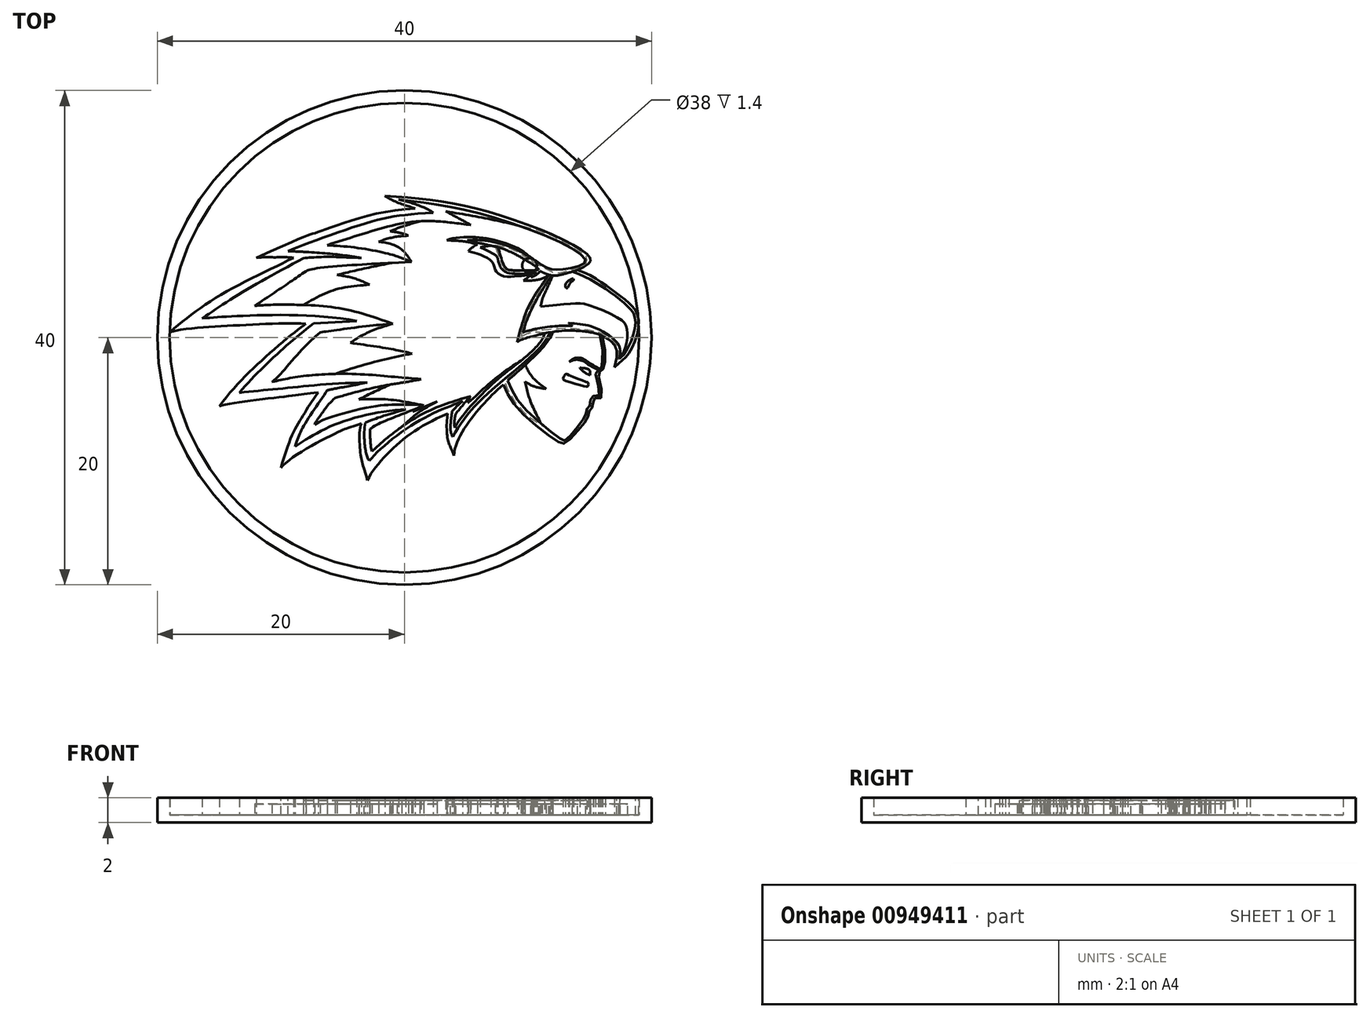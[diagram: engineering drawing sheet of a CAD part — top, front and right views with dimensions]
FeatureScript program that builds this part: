
annotation { "Feature Type Name" : "Feature", "Feature Type Description" : "" }
export const myFeature = defineFeature(function(context is Context, id is Id, definition is map)
    precondition{}
    {
        {
            var Q0;
            Q0=qCreatedBy(makeId("Top.planeOp"),FACE);
            var sketch = newSketch(context, id + "F0", { "sketchPlane" : qUnion([Q0])});
            skCircle(sketch, "E0", {"center": v(0, 0) * mm, "radius": 20 * mm});
            skSolve(sketch);
        }
        {
            var Q0;
            Q0=makeQuery(id+"F0.imprint","IMPRINT",FACE,{"disambiguationData":[TD([[makeQuery(id+"F0.imprint","IMPRINT",EDGE,{"derivedFrom":sQuery(id+"F0.wireOp",EDGE,"E0")}),1.0]])]});
            extrude(context, id + "F1", {"entities" : qUnion([Q0]), "oppositeDirection" : true, "depth" : 0.6 * mm, "offsetDistance" : 25 * mm});
        }
        {
            var Q0;
            Q0=qCreatedBy(makeId("Top.planeOp"),FACE);
            var sketch = newSketch(context, id + "F2", { "sketchPlane" : qUnion([Q0])});
            skCircle(sketch, "E1", {"center": v(0, 0) * mm, "radius": 20 * mm});
            skCircle(sketch, "E2", {"center": v(0, 0) * mm, "radius": 19 * mm});
            skSolve(sketch);
        }
        {
            var Q0;
            Q0=makeQuery(id+"F2.imprint","IMPRINT",FACE,{"disambiguationData":[TD([[makeQuery(id+"F2.imprint","IMPRINT",EDGE,{"derivedFrom":sQuery(id+"F2.wireOp",EDGE,"E1")}),1.0]])]});
            extrude(context, id + "F3", {"entities" : qUnion([Q0]), "operationType" : NewBodyOperationType.ADD, "depth" : 1.4 * mm, "offsetDistance" : 25 * mm});
        }
        {
            var Q0;
            Q0=qCreatedBy(makeId("Top.planeOp"),FACE);
            var sketch = newSketch(context, id + "F4", { "sketchPlane" : qUnion([Q0])});
            skFitSpline(sketch, "E3", {"points": [v(-1.58, 11.46) * mm, v(7.72, 9.91) * mm, v(15.05, 6.42) * mm, v(14, 5.46) * mm], "startDerivative": vector(21.52, -1.26) * mm, "endDerivative": vector(-13.3, -6.93) * mm});
            skFitSpline(sketch, "E4", {"points": [v(3.5, -6.16) * mm, v(-0.78, -8.83) * mm, v(-3, -11.54) * mm], "startDerivative": vector(-10.76, -4.46) * mm, "endDerivative": vector(-2.73, -5.76) * mm});
            skFitSpline(sketch, "E5", {"points": [v(-3, -11.54) * mm, v(-3.55, -9.5) * mm, v(-3.5, -6.96) * mm], "startDerivative": vector(-2.35, 7.78) * mm, "endDerivative": vector(1.35, 3.27) * mm});
            skFitSpline(sketch, "E6", {"points": [v(-3.5, -6.96) * mm, v(-5.27, -7.6) * mm, v(-10, -10.54) * mm], "startDerivative": vector(-9.15, -3.1) * mm, "endDerivative": vector(-2.97, -4.21) * mm});
            skFitSpline(sketch, "E7", {"points": [v(-10, -10.54) * mm, v(-8.32, -6.48) * mm, v(-7, -4.44) * mm], "startDerivative": vector(3.25, 11.93) * mm, "endDerivative": vector(2.66, 3.7) * mm});
            skFitSpline(sketch, "E8", {"points": [v(-7, -4.44) * mm, v(-9.47, -4.75) * mm, v(-15, -5.54) * mm], "startDerivative": vector(-8.24, -0.84) * mm, "endDerivative": vector(-4.12, -1.43) * mm});
            skFitSpline(sketch, "E9", {"points": [v(-15, -5.54) * mm, v(-11, -1.34) * mm, v(-8, 1.1) * mm], "startDerivative": vector(6.54, 8.64) * mm, "endDerivative": vector(3.53, 2.33) * mm});
            skFitSpline(sketch, "E10", {"points": [v(-8, 1.1) * mm, v(-13.7, 0.98) * mm, v(-19, 0.46) * mm], "startDerivative": vector(-8.4, 0.77) * mm, "endDerivative": vector(-10.04, -2.22) * mm});
            skFitSpline(sketch, "E11", {"points": [v(-19, 0.46) * mm, v(-14.13, 3.88) * mm, v(-8, 7.06) * mm], "startDerivative": vector(8.8, 7.31) * mm, "endDerivative": vector(6.6, 4.65) * mm});
            skFitSpline(sketch, "E12", {"points": [v(-12, 6.46) * mm, v(-6.88, 8.58) * mm, v(0.86, 10.46) * mm], "startDerivative": vector(30.08, 13.67) * mm, "endDerivative": vector(18.85, 0.85) * mm});
            skFitSpline(sketch, "E13", {"points": [v(0.86, 10.46) * mm, v(-0.78, 11.03) * mm, v(-1.58, 11.46) * mm], "startDerivative": vector(-2.07, 0.66) * mm, "endDerivative": vector(-0.97, 0.57) * mm});
            skFitSpline(sketch, "E14", {"points": [v(3.5, -6.16) * mm, v(3.53, -8.34) * mm, v(4, -9.54) * mm], "startDerivative": vector(-0.77, -3.97) * mm, "endDerivative": vector(1.6, -4.4) * mm});
            skFitSpline(sketch, "E15", {"points": [v(4, -9.54) * mm, v(5.91, -5.93) * mm, v(9.09, -2.82) * mm, v(12, 0.46) * mm], "startDerivative": vector(0.54, 10.48) * mm, "endDerivative": vector(2.95, 8.84) * mm});
            skFitSpline(sketch, "E16", {"points": [v(-9, 6.46) * mm, v(-10.52, 6.5) * mm, v(-12, 6.46) * mm], "startDerivative": vector(-3.14, 0.42) * mm, "endDerivative": vector(-2.86, -0.43) * mm});
            skFitSpline(sketch, "E17", {"points": [v(14, 5.46) * mm, v(16.43, 4.12) * mm, v(18.07, 2.88) * mm, v(18.94, 1.52) * mm, v(18.18, -1.26) * mm, v(17, -2.4) * mm], "startDerivative": vector(12.4, -3.48) * mm, "endDerivative": vector(-8.18, -8.07) * mm});
            skFitSpline(sketch, "E18", {"points": [v(17, -2.4) * mm, v(17.07, -0.75) * mm, v(15.73, 0.25) * mm, v(14.63, 0.5) * mm, v(12, 0.46) * mm], "startDerivative": vector(1.76, 6.26) * mm, "endDerivative": vector(-11.27, -1.86) * mm});
            skFitSpline(sketch, "E19", {"points": [v(11, 5.38) * mm, v(9.78, 6.3) * mm, v(7, 7.43) * mm], "startDerivative": vector(-2.8, 3.17) * mm, "endDerivative": vector(-5.7, 0.83) * mm});
            skFitSpline(sketch, "E20", {"points": [v(7, 7.43) * mm, v(7.74, 5.78) * mm, v(8, 5.43) * mm, v(8.44, 5.22) * mm, v(10.45, 5.2) * mm, v(10.9, 5.29) * mm, v(11, 5.38) * mm], "startDerivative": vector(6.03, -7.57) * mm, "endDerivative": vector(2.14, 2.82) * mm});
            skCircle(sketch, "E21", {"center": v(10.12, 5.84) * mm, "radius": 0.6 * mm});
            skFitSpline(sketch, "E22", {"points": [v(8, -3.8) * mm, v(9.3, -5.87) * mm, v(12.45, -8.44) * mm, v(13, -8.54) * mm, v(14.39, -7.12) * mm, v(14.92, -6.25) * mm, v(15.02, -5.8) * mm, v(15.28, -5.52) * mm, v(15.34, -4.9) * mm, v(15.93, -4.86) * mm, v(15.7, -2.86) * mm, v(15.92, -2.64) * mm, v(16.14, -2.4) * mm, v(16, 0.14) * mm], "startDerivative": vector(7.5, -17.46) * mm, "endDerivative": vector(-8.07, 26.27) * mm});
            skFitSpline(sketch, "E23", {"points": [v(15.02, -3.03) * mm, v(14.56, -2.8) * mm, v(14.2, -2.44) * mm], "startDerivative": vector(-1.12, 0.33) * mm, "endDerivative": vector(-0.33, 0.79) * mm});
            skFitSpline(sketch, "E24", {"points": [v(14.2, -2.44) * mm, v(14.57, -2.47) * mm, v(14.94, -2.61) * mm, v(15.04, -2.8) * mm, v(15.02, -3.03) * mm], "startDerivative": vector(1.37, -0.38) * mm, "endDerivative": vector(-0.15, -0.97) * mm});
            skFitSpline(sketch, "E25", {"points": [v(15.68, -2.55) * mm, v(15.48, -2.5) * mm, v(14.93, -2.22) * mm, v(14.67, -2.02) * mm, v(14.03, -1.79) * mm, v(13.34, -1.95) * mm], "startDerivative": vector(-2.24, 0.34) * mm, "endDerivative": vector(-2.61, -1.2) * mm});
            skFitSpline(sketch, "E26", {"points": [v(13.34, -1.95) * mm, v(13.86, -1.65) * mm, v(14.3, -1.65) * mm, v(14.57, -1.77) * mm, v(15.1, -2.13) * mm, v(15.55, -2.4) * mm, v(15.89, -2.49) * mm], "startDerivative": vector(2.26, 2.4) * mm, "endDerivative": vector(2.1, 0.6) * mm});
            skFitSpline(sketch, "E27", {"points": [v(15.68, -2.55) * mm, v(15.8, -2.54) * mm, v(15.89, -2.49) * mm], "startDerivative": vector(0.25, -0.06) * mm, "endDerivative": vector(0.25, 0.3) * mm});
            skFitSpline(sketch, "E28", {"points": [v(14.52, -3.93) * mm, v(12.97, -3.46) * mm, v(12.85, -3.33) * mm, v(12.9, -3.2) * mm, v(12.98, -3) * mm, v(13.07, -2.94) * mm, v(13.22, -3) * mm, v(14.68, -3.57) * mm, v(14.86, -3.66) * mm, v(14.9, -3.76) * mm, v(14.84, -3.93) * mm, v(14.78, -3.97) * mm, v(14.52, -3.93) * mm]});
            skFitSpline(sketch, "E29", {"points": [v(12, 0.46) * mm, v(10.73, 0.2) * mm, v(9.12, -0.4) * mm], "startDerivative": vector(-4.79, -0.65) * mm, "endDerivative": vector(-1.75, -1.76) * mm});
            skFitSpline(sketch, "E30", {"points": [v(9.12, -0.4) * mm, v(10.04, 2.5) * mm, v(11.7, 5.07) * mm], "startDerivative": vector(1.47, 5.98) * mm, "endDerivative": vector(3.7, 4.95) * mm});
            skFitSpline(sketch, "E31", {"points": [v(14, 5.46) * mm, v(12.41, 5.04) * mm, v(11.7, 5.07) * mm, v(11, 5.38) * mm], "startDerivative": vector(-4.1, -1.19) * mm, "endDerivative": vector(-2.43, 1.23) * mm});
            skFitSpline(sketch, "E32", {"points": [v(7, 7.43) * mm, v(5.97, 7.67) * mm, v(5.07, 7.87) * mm], "startDerivative": vector(-2.03, 0.53) * mm, "endDerivative": vector(-1.84, 0.4) * mm});
            skFitSpline(sketch, "E33", {"points": [v(5.07, 7.87) * mm, v(6.4, 7.87) * mm, v(9.35, 7) * mm, v(11.6, 5.62) * mm, v(12.86, 5.54) * mm, v(14.66, 6.18) * mm, v(7.76, 9.56) * mm, v(-0.49, 11.17) * mm], "startDerivative": vector(13.05, 0.9) * mm, "endDerivative": vector(-32.62, 3.92) * mm});
            skFitSpline(sketch, "E34", {"points": [v(-0.49, 11.17) * mm, v(0.93, 10.77) * mm, v(2.33, 10.11) * mm], "startDerivative": vector(2.94, -0.6) * mm, "endDerivative": vector(1.78, -1.4) * mm});
            skFitSpline(sketch, "E35", {"points": [v(2.33, 10.11) * mm, v(-3.07, 9.27) * mm, v(-9.44, 7) * mm], "startDerivative": vector(-15.85, -1) * mm, "endDerivative": vector(-7.4, -3.02) * mm});
            skFitSpline(sketch, "E36", {"points": [v(-9.44, 7) * mm, v(-6.18, 6.8) * mm, v(-3.48, 6.46) * mm], "startDerivative": vector(6.38, -0.27) * mm, "endDerivative": vector(5.53, -0.87) * mm});
            skFitSpline(sketch, "E37", {"points": [v(-3.48, 6.46) * mm, v(-6.21, 6.54) * mm, v(-8.18, 6.43) * mm], "startDerivative": vector(-6.33, 0.08) * mm, "endDerivative": vector(-3.05, -0.33) * mm});
            skFitSpline(sketch, "E38", {"points": [v(-8.18, 6.43) * mm, v(-13.5, 3.44) * mm, v(-16.37, 1.55) * mm], "startDerivative": vector(-9.86, -5.27) * mm, "endDerivative": vector(-6.1, -4.23) * mm});
            skFitSpline(sketch, "E39", {"points": [v(-16.37, 1.55) * mm, v(-13.5, 1.75) * mm, v(-3.85, 1.35) * mm], "startDerivative": vector(6.8, 0.6) * mm, "endDerivative": vector(14.41, -2.83) * mm});
            skFitSpline(sketch, "E40", {"points": [v(-3.85, 1.35) * mm, v(-7.35, 1.14) * mm], "startDerivative": vector(-3.5, -0.2) * mm, "endDerivative": vector(-3.5, -0.2) * mm});
            skFitSpline(sketch, "E41", {"points": [v(-7.35, 1.14) * mm, v(-10.41, -1.43) * mm, v(-13.36, -4.46) * mm], "startDerivative": vector(-6.68, -4.88) * mm, "endDerivative": vector(-5.36, -6.32) * mm});
            skFitSpline(sketch, "E42", {"points": [v(-13.36, -4.46) * mm, v(-9.36, -4.06) * mm, v(-3.02, -3.64) * mm], "startDerivative": vector(8.78, 0.94) * mm, "endDerivative": vector(14.42, 0.16) * mm});
            skFitSpline(sketch, "E43", {"points": [v(-3.02, -3.64) * mm, v(-5.54, -4.12) * mm, v(-6.24, -4.25) * mm], "startDerivative": vector(-4.48, -0.91) * mm, "endDerivative": vector(-1.64, -0.24) * mm});
            skFitSpline(sketch, "E44", {"points": [v(-6.24, -4.25) * mm, v(-8.21, -7.25) * mm, v(-8.87, -8.8) * mm], "startDerivative": vector(-3.02, -4.33) * mm, "endDerivative": vector(-1.83, -4.96) * mm});
            skFitSpline(sketch, "E45", {"points": [v(-8.87, -8.8) * mm, v(-5.6, -7.02) * mm, v(0.1, -5.81) * mm], "startDerivative": vector(6.74, 4.12) * mm, "endDerivative": vector(9.55, 0.33) * mm});
            skFitSpline(sketch, "E46", {"points": [v(0.1, -5.81) * mm, v(-1.02, -6.13) * mm, v(-3.18, -6.9) * mm], "startDerivative": vector(-4.07, -1.11) * mm, "endDerivative": vector(-5.58, -2.4) * mm});
            skFitSpline(sketch, "E47", {"points": [v(-3.18, -6.9) * mm, v(-3.14, -9.14) * mm, v(-2.84, -9.97) * mm], "startDerivative": vector(-0.7, -4.41) * mm, "endDerivative": vector(1.32, -1.52) * mm});
            skFitSpline(sketch, "E48", {"points": [v(-2.84, -9.97) * mm, v(0.78, -6.97) * mm, v(4.7, -5.14) * mm], "startDerivative": vector(3.54, 4.6) * mm, "endDerivative": vector(7.5, 2.99) * mm});
            skFitSpline(sketch, "E49", {"points": [v(4.7, -5.14) * mm, v(3.85, -5.96) * mm], "startDerivative": vector(-1.54, -1.24) * mm, "endDerivative": vector(-0.85, -0.81) * mm});
            skFitSpline(sketch, "E50", {"points": [v(3.85, -5.96) * mm, v(3.74, -7.58) * mm, v(3.91, -8.04) * mm], "startDerivative": vector(-0.38, -2.91) * mm, "endDerivative": vector(0.59, -1.08) * mm});
            skFitSpline(sketch, "E51", {"points": [v(3.91, -8.04) * mm, v(5.56, -5.69) * mm, v(8.66, -2.88) * mm, v(11.8, 0.43) * mm], "startDerivative": vector(4.66, 8.5) * mm, "endDerivative": vector(3.92, 9.27) * mm});
            skFitSpline(sketch, "E52", {"points": [v(11.8, 0.43) * mm, v(12, 0.46) * mm], "startDerivative": vector(0.2, 0.03) * mm, "endDerivative": vector(0.2, 0.03) * mm});
            skFitSpline(sketch, "E53", {"points": [v(11.92, 5.03) * mm, v(10.4, 2.5) * mm, v(9.6, 0.43) * mm], "startDerivative": vector(-3.21, -4.76) * mm, "endDerivative": vector(-1.06, -4.44) * mm});
            skFitSpline(sketch, "E54", {"points": [v(9.6, 0.43) * mm, v(10.45, 0.67) * mm, v(12.21, 0.92) * mm, v(13.6, 0.96) * mm], "startDerivative": vector(2.74, 0.91) * mm, "endDerivative": vector(3.8, 0) * mm});
            skFitSpline(sketch, "E55", {"points": [v(13.6, 0.96) * mm, v(13.29, 1.17) * mm], "startDerivative": vector(-0.45, 0.21) * mm, "endDerivative": vector(-0.45, 0.21) * mm});
            skFitSpline(sketch, "E56", {"points": [v(13.29, 1.17) * mm, v(14.52, 1.05) * mm, v(15.83, 0.62) * mm, v(17.37, -0.67) * mm, v(17.4, -1.7) * mm], "startDerivative": vector(5.3, -0.38) * mm, "endDerivative": vector(-0.98, -4.8) * mm});
            skFitSpline(sketch, "E57", {"points": [v(17.4, -1.7) * mm, v(17.94, -1.12) * mm, v(18.7, 1.36) * mm, v(18, 2.6) * mm, v(16.13, 4.03) * mm, v(13.6, 5.34) * mm], "startDerivative": vector(3.88, 3.06) * mm, "endDerivative": vector(-12.32, 4.18) * mm});
            skFitSpline(sketch, "E58", {"points": [v(7.58, 7.31) * mm, v(8.08, 5.8) * mm, v(8.4, 5.5) * mm, v(8.78, 5.45) * mm, v(10.88, 5.51) * mm], "startDerivative": vector(1.53, -5.22) * mm, "endDerivative": vector(2.76, 1.11) * mm});
            skFitSpline(sketch, "E59", {"points": [v(7.48, 6.59) * mm, v(6.84, 6.98) * mm, v(6.14, 7.3) * mm], "startDerivative": vector(-1.21, 0.84) * mm, "endDerivative": vector(-1.25, 0.39) * mm});
            skFitSpline(sketch, "E60", {"points": [v(7, 7.43) * mm, v(6.54, 7.38) * mm, v(6.14, 7.3) * mm], "startDerivative": vector(-0.92, 0.03) * mm, "endDerivative": vector(-1.04, -0.3) * mm});
            skFitSpline(sketch, "E61", {"points": [v(11, 5.38) * mm, v(10.6, 5.04) * mm, v(10.25, 4.9) * mm], "startDerivative": vector(-0.74, -0.71) * mm, "endDerivative": vector(-0.76, -0.25) * mm});
            skFitSpline(sketch, "E62", {"points": [v(10.25, 4.9) * mm, v(10.65, 5.17) * mm, v(10.88, 5.51) * mm], "startDerivative": vector(0.83, 0.5) * mm, "endDerivative": vector(0.41, 0.76) * mm});
            skFitSpline(sketch, "E63", {"points": [v(13.68, 4.76) * mm, v(13.18, 4.53) * mm, v(13.02, 4.13) * mm, v(13.16, 4) * mm, v(13.46, 4.47) * mm, v(13.69, 4.66) * mm, v(13.68, 4.76) * mm]});
            skFitSpline(sketch, "E64", {"points": [v(15.8, 0.23) * mm, v(15.96, -2.32) * mm, v(15.87, -2.55) * mm, v(15.5, -2.72) * mm, v(15.76, -4.68) * mm, v(15.14, -4.76) * mm, v(15.04, -5.45) * mm, v(14.8, -5.7) * mm, v(14.68, -6.2) * mm, v(14.23, -6.92) * mm, v(13, -8.3) * mm, v(12.58, -8.17) * mm, v(9.59, -5.6) * mm, v(8.35, -3.48) * mm], "startDerivative": vector(10.2, -30.63) * mm, "endDerivative": vector(-7.66, 17.6) * mm});
            skFitSpline(sketch, "E65", {"points": [v(10.7, 5.68) * mm, v(10.67, 6.08) * mm, v(10.45, 6.34) * mm], "startDerivative": vector(0.04, 0.82) * mm, "endDerivative": vector(-0.55, 0.49) * mm});
            skFitSpline(sketch, "E66", {"points": [v(3.5, -6.16) * mm, v(3.85, -5.96) * mm], "startDerivative": vector(0.35, 0.2) * mm, "endDerivative": vector(0.35, 0.2) * mm});
            skFitSpline(sketch, "E67", {"points": [v(-2.84, -9.97) * mm, v(-3, -11.54) * mm], "startDerivative": vector(-0.16, -1.59) * mm, "endDerivative": vector(-0.16, -1.59) * mm});
            skFitSpline(sketch, "E68", {"points": [v(-3.18, -6.9) * mm, v(-3.5, -6.96) * mm], "startDerivative": vector(-0.31, -0.06) * mm, "endDerivative": vector(-0.31, -0.06) * mm});
            skFitSpline(sketch, "E69", {"points": [v(-8.87, -8.8) * mm, v(-10, -10.54) * mm], "startDerivative": vector(-1.13, -1.75) * mm, "endDerivative": vector(-1.13, -1.75) * mm});
            skFitSpline(sketch, "E70", {"points": [v(-7, -4.44) * mm, v(-6.24, -4.25) * mm], "startDerivative": vector(0.76, 0.19) * mm, "endDerivative": vector(0.76, 0.19) * mm});
            skFitSpline(sketch, "E71", {"points": [v(-13.36, -4.46) * mm, v(-15, -5.54) * mm], "startDerivative": vector(-1.63, -1.1) * mm, "endDerivative": vector(-1.63, -1.1) * mm});
            skFitSpline(sketch, "E72", {"points": [v(-8, 1.1) * mm, v(-7.35, 1.14) * mm], "startDerivative": vector(0.65, 0.03) * mm, "endDerivative": vector(0.65, 0.03) * mm});
            skFitSpline(sketch, "E73", {"points": [v(-16.37, 1.55) * mm, v(-19, 0.46) * mm], "startDerivative": vector(-2.63, -1.1) * mm, "endDerivative": vector(-2.63, -1.1) * mm});
            skFitSpline(sketch, "E74", {"points": [v(-9, 6.46) * mm, v(-8.18, 6.43) * mm], "startDerivative": vector(0.82, -0.01) * mm, "endDerivative": vector(0.82, -0.01) * mm});
            skFitSpline(sketch, "E75", {"points": [v(-9.44, 7) * mm, v(-12, 6.46) * mm], "startDerivative": vector(-2.56, -0.56) * mm, "endDerivative": vector(-2.56, -0.56) * mm});
            skFitSpline(sketch, "E76", {"points": [v(0.86, 10.46) * mm, v(2.33, 10.11) * mm], "startDerivative": vector(1.48, -0.33) * mm, "endDerivative": vector(1.48, -0.33) * mm});
            skFitSpline(sketch, "E77", {"points": [v(-0.49, 11.17) * mm, v(-1.58, 11.46) * mm], "startDerivative": vector(-1.1, 0.27) * mm, "endDerivative": vector(-1.1, 0.27) * mm});
            skFitSpline(sketch, "E78", {"points": [v(13.6, 5.34) * mm, v(14, 5.46) * mm], "startDerivative": vector(0.4, 0.12) * mm, "endDerivative": vector(0.4, 0.12) * mm});
            skFitSpline(sketch, "E79", {"points": [v(7, 7.43) * mm, v(7.58, 7.31) * mm], "startDerivative": vector(0.57, -0.12) * mm, "endDerivative": vector(0.57, -0.12) * mm});
            skSolve(sketch);
        }
        {
            var Q0;
            {var subQ2=sQuery(id+"F4.wireOp",EDGE,"E59");Q0=makeQuery(id+"F4.imprint","IMPRINT",FACE,{"disambiguationData":[TD([[makeQuery(id+"F4.imprint","IMPRINT",EDGE,{"derivedFrom":subQ2}),-1.0]])]});}
            var Q1;
            Q1=makeQuery(id+"F4.imprint","IMPRINT",FACE,{"disambiguationData":[TD([[makeQuery(id+"F4.imprint","IMPRINT",EDGE,{"derivedFrom":sQuery(id+"F4.wireOp",EDGE,"E63")}),1.0]])]});
            var Q2;
            {var subQ0=sQuery(id+"F4.wireOp",EDGE,"E32");Q2=makeQuery(id+"F4.imprint","IMPRINT",FACE,{"disambiguationData":[TD([[makeQuery(id+"F4.imprint","IMPRINT",EDGE,{"derivedFrom":subQ0}),-1.0]])]});}
            var Q3;
            {var subQ0=sQuery(id+"F4.wireOp",EDGE,"E79");Q3=makeQuery(id+"F4.imprint","IMPRINT",FACE,{"disambiguationData":[TD([[makeQuery(id+"F4.imprint","IMPRINT",EDGE,{"derivedFrom":subQ0}),-1.0]])]});}
            var Q4;
            Q4=makeQuery(id+"F4.imprint","IMPRINT",FACE,{"disambiguationData":[TD([[makeQuery(id+"F4.imprint","IMPRINT",EDGE,{"derivedFrom":sQuery(id+"F4.wireOp",EDGE,"E3")}),-1.0]])]});
            var Q5;
            {var subQ0=sQuery(id+"F4.wireOp",EDGE,"E62");var subQ1=sQuery(id+"F4.wireOp",EDGE,"E20");var subQ2=makeQuery(id+"F4.imprint","INTERSECT",VERTEX,{"derivedFrom":[subQ1,subQ0]});Q5=makeQuery(id+"F4.imprint","IMPRINT",FACE,{"disambiguationData":[TD([[makeQuery(id+"F4.imprint","IMPRINT",EDGE,{"disambiguationData":[TD([[subQ2,-1.0]])],"derivedFrom":subQ1}),-1.0]])]});}
            var Q6;
            {var subQ1=sQuery(id+"F4.wireOp",EDGE,"E20");var subQ4=sQuery(id+"F4.wireOp",EDGE,"E62");var subQ6=makeQuery(id+"F4.imprint","INTERSECT",VERTEX,{"derivedFrom":[subQ1,subQ4]});Q6=makeQuery(id+"F4.imprint","IMPRINT",FACE,{"disambiguationData":[TD([[makeQuery(id+"F4.imprint","IMPRINT",EDGE,{"disambiguationData":[TD([[subQ6,-1.0]])],"derivedFrom":subQ1}),1.0]])]});}
            var Q7;
            {var subQ0=sQuery(id+"F4.wireOp",EDGE,"E21");var subQ1=sQuery(id+"F4.wireOp",EDGE,"E19");var subQ3=makeQuery(id+"F4.imprint","INTERSECT",VERTEX,{"derivedFrom":[subQ1,subQ0]});Q7=makeQuery(id+"F4.imprint","IMPRINT",FACE,{"disambiguationData":[TD([[makeQuery(id+"F4.imprint","IMPRINT",EDGE,{"disambiguationData":[TD([[subQ3,-1.0]])],"derivedFrom":subQ0}),1.0]])]});}
            var Q8;
            {var subQ4=sQuery(id+"F4.wireOp",EDGE,"E14");Q8=makeQuery(id+"F4.imprint","IMPRINT",FACE,{"disambiguationData":[TD([[makeQuery(id+"F4.imprint","IMPRINT",EDGE,{"derivedFrom":subQ4}),1.0]])]});}
            var Q9;
            {var subQ0=sQuery(id+"F4.wireOp",EDGE,"E22");Q9=makeQuery(id+"F4.imprint","IMPRINT",FACE,{"disambiguationData":[TD([[makeQuery(id+"F4.imprint","IMPRINT",EDGE,{"derivedFrom":subQ0}),1.0]])]});}
            var Q10;
            Q10=makeQuery(id+"F4.imprint","IMPRINT",FACE,{"disambiguationData":[TD([[makeQuery(id+"F4.imprint","IMPRINT",EDGE,{"derivedFrom":sQuery(id+"F4.wireOp",EDGE,"E23")}),-1.0]])]});
            var Q11;
            Q11=makeQuery(id+"F4.imprint","IMPRINT",FACE,{"disambiguationData":[TD([[makeQuery(id+"F4.imprint","IMPRINT",EDGE,{"derivedFrom":sQuery(id+"F4.wireOp",EDGE,"E28")}),-1.0]])]});
            var Q12;
            Q12=makeQuery(id+"F4.imprint","IMPRINT",FACE,{"disambiguationData":[TD([[makeQuery(id+"F4.imprint","IMPRINT",EDGE,{"derivedFrom":sQuery(id+"F4.wireOp",EDGE,"E25")}),-1.0]])]});
            var Q13;
            Q13=makeQuery(id+"F4.imprint","IMPRINT",FACE,{"disambiguationData":[TD([[makeQuery(id+"F4.imprint","IMPRINT",EDGE,{"derivedFrom":sQuery(id+"F4.wireOp",EDGE,"E4")}),-1.0]])]});
            var Q14;
            Q14=makeQuery(id+"F4.imprint","IMPRINT",FACE,{"disambiguationData":[TD([[makeQuery(id+"F4.imprint","IMPRINT",EDGE,{"derivedFrom":sQuery(id+"F4.wireOp",EDGE,"E5")}),-1.0]])]});
            var Q15;
            Q15=makeQuery(id+"F4.imprint","IMPRINT",FACE,{"disambiguationData":[TD([[makeQuery(id+"F4.imprint","IMPRINT",EDGE,{"derivedFrom":sQuery(id+"F4.wireOp",EDGE,"E6")}),-1.0]])]});
            var Q16;
            Q16=makeQuery(id+"F4.imprint","IMPRINT",FACE,{"disambiguationData":[TD([[makeQuery(id+"F4.imprint","IMPRINT",EDGE,{"derivedFrom":sQuery(id+"F4.wireOp",EDGE,"E7")}),-1.0]])]});
            var Q17;
            Q17=makeQuery(id+"F4.imprint","IMPRINT",FACE,{"disambiguationData":[TD([[makeQuery(id+"F4.imprint","IMPRINT",EDGE,{"derivedFrom":sQuery(id+"F4.wireOp",EDGE,"E8")}),-1.0]])]});
            var Q18;
            Q18=makeQuery(id+"F4.imprint","IMPRINT",FACE,{"disambiguationData":[TD([[makeQuery(id+"F4.imprint","IMPRINT",EDGE,{"derivedFrom":sQuery(id+"F4.wireOp",EDGE,"E9")}),-1.0]])]});
            var Q19;
            Q19=makeQuery(id+"F4.imprint","IMPRINT",FACE,{"disambiguationData":[TD([[makeQuery(id+"F4.imprint","IMPRINT",EDGE,{"derivedFrom":sQuery(id+"F4.wireOp",EDGE,"E10")}),-1.0]])]});
            var Q20;
            Q20=makeQuery(id+"F4.imprint","IMPRINT",FACE,{"disambiguationData":[TD([[makeQuery(id+"F4.imprint","IMPRINT",EDGE,{"derivedFrom":sQuery(id+"F4.wireOp",EDGE,"E11")}),-1.0]])]});
            var Q21;
            Q21=makeQuery(id+"F4.imprint","IMPRINT",FACE,{"disambiguationData":[TD([[makeQuery(id+"F4.imprint","IMPRINT",EDGE,{"derivedFrom":sQuery(id+"F4.wireOp",EDGE,"E12")}),-1.0]])]});
            var Q22;
            Q22=makeQuery(id+"F4.imprint","IMPRINT",FACE,{"disambiguationData":[TD([[makeQuery(id+"F4.imprint","IMPRINT",EDGE,{"derivedFrom":sQuery(id+"F4.wireOp",EDGE,"E13")}),-1.0]])]});
            var Q23;
            Q23=makeQuery(id+"F4.imprint","IMPRINT",FACE,{"disambiguationData":[TD([[makeQuery(id+"F4.imprint","IMPRINT",EDGE,{"derivedFrom":sQuery(id+"F4.wireOp",EDGE,"E16")}),-1.0]])]});
            extrude(context, id + "F5", {"entities" : qUnion([Q0, Q1, Q2, Q3, Q4, Q5, Q6, Q7, Q8, Q9, Q10, Q11, Q12, Q13, Q14, Q15, Q16, Q17, Q18, Q19, Q20, Q21, Q22, Q23]), "depth" : 1.4 * mm, "offsetDistance" : 25 * mm});
        }
        {
            var Q0;
            {var subQ1=sQuery(id+"F4.wireOp",EDGE,"E21");var subQ3=sQuery(id+"F4.wireOp",EDGE,"E65");var subQ8=makeQuery(id+"F4.imprint","INTERSECT",VERTEX,{"disambiguationData":[OD(1.0)],"derivedFrom":[subQ1,subQ3]});Q0=makeQuery(id+"F4.imprint","IMPRINT",FACE,{"disambiguationData":[TD([[makeQuery(id+"F4.imprint","IMPRINT",EDGE,{"disambiguationData":[TD([[subQ8,1.0]])],"derivedFrom":subQ1}),1.0]])]});}
            var Q1;
            {var subQ0=sQuery(id+"F4.wireOp",EDGE,"E58");var subQ1=sQuery(id+"F4.wireOp",EDGE,"E21");var subQ2=makeQuery(id+"F4.imprint","INTERSECT",VERTEX,{"disambiguationData":[OD(0.0)],"derivedFrom":[subQ1,subQ0]});Q1=makeQuery(id+"F4.imprint","IMPRINT",FACE,{"disambiguationData":[TD([[makeQuery(id+"F4.imprint","IMPRINT",EDGE,{"disambiguationData":[TD([[subQ2,-1.0]])],"derivedFrom":subQ1}),1.0]])]});}
            var Q2;
            {var subQ3=sQuery(id+"F4.wireOp",EDGE,"E17");Q2=makeQuery(id+"F4.imprint","IMPRINT",FACE,{"disambiguationData":[TD([[makeQuery(id+"F4.imprint","IMPRINT",EDGE,{"derivedFrom":subQ3}),-1.0]])]});}
            extrude(context, id + "F6", {"entities" : qUnion([Q0, Q1, Q2]), "depth" : 1.4 * mm, "offsetDistance" : 25 * mm});
        }
        {
            var Q0;
            Q0=qCreatedBy(makeId("Top.planeOp"),FACE);
            var sketch = newSketch(context, id + "F7", { "sketchPlane" : qUnion([Q0])});
            skFitSpline(sketch, "E80", {"points": [v(9.24, 9.07) * mm, v(6.48, 9.68) * mm, v(3.36, 10.21) * mm], "startDerivative": vector(-5.59, 1.3) * mm, "endDerivative": vector(-6.18, 0.99) * mm});
            skFitSpline(sketch, "E81", {"points": [v(3.36, 10.21) * mm, v(4.58, 9.55) * mm, v(5.36, 9.11) * mm], "startDerivative": vector(2.33, -1.25) * mm, "endDerivative": vector(1.65, -0.94) * mm});
            skFitSpline(sketch, "E82", {"points": [v(5.36, 9.11) * mm, v(1.84, 9.43) * mm, v(-0.77, 9.11) * mm, v(-3.65, 8.3) * mm, v(-6.26, 7.48) * mm], "startDerivative": vector(-13.44, 1.75) * mm, "endDerivative": vector(-10.65, -3.43) * mm});
            skFitSpline(sketch, "E83", {"points": [v(-6.26, 7.48) * mm, v(-3.77, 7.26) * mm, v(-1.33, 6.8) * mm, v(-0.6, 6.58) * mm], "startDerivative": vector(6.13, -0.37) * mm, "endDerivative": vector(2.83, -0.95) * mm});
            skFitSpline(sketch, "E84", {"points": [v(-0.6, 6.58) * mm, v(0.57, 6.14) * mm], "startDerivative": vector(1.17, -0.44) * mm, "endDerivative": vector(1.17, -0.44) * mm});
            skFitSpline(sketch, "E85", {"points": [v(0.57, 6.14) * mm, v(-2.73, 5.95) * mm, v(-7.32, 5.57) * mm, v(-7.98, 5.39) * mm], "startDerivative": vector(-7.72, -0.4) * mm, "endDerivative": vector(-2.75, -1.12) * mm});
            skFitSpline(sketch, "E86", {"points": [v(-7.98, 5.39) * mm, v(-9.69, 4.2) * mm, v(-12.13, 2.57) * mm], "startDerivative": vector(-3.57, -2.49) * mm, "endDerivative": vector(-4.7, -3.13) * mm});
            skFitSpline(sketch, "E87", {"points": [v(-12.13, 2.57) * mm, v(-9, 2.66) * mm, v(-4.97, 2.32) * mm, v(-0.94, 1.13) * mm], "startDerivative": vector(10.13, 1) * mm, "endDerivative": vector(11.36, -3.84) * mm});
            skFitSpline(sketch, "E88", {"points": [v(-0.94, 1.13) * mm, v(-3.24, 0.9) * mm, v(-5.8, 0.57) * mm, v(-6.83, 0.42) * mm], "startDerivative": vector(-5.98, -0.5) * mm, "endDerivative": vector(-3.65, -0.52) * mm});
            skFitSpline(sketch, "E89", {"points": [v(-6.83, 0.42) * mm, v(-8.44, -1.12) * mm, v(-10.2, -3.12) * mm, v(-10.71, -3.58) * mm], "startDerivative": vector(-4.12, -3.65) * mm, "endDerivative": vector(-2.1, -1.68) * mm});
            skFitSpline(sketch, "E90", {"points": [v(-10.71, -3.58) * mm, v(-8.59, -3.17) * mm, v(-4.83, -2.93) * mm, v(-1.19, -3.15) * mm, v(1.35, -3.37) * mm], "startDerivative": vector(9.22, 2.1) * mm, "endDerivative": vector(10.55, -0.9) * mm});
            skFitSpline(sketch, "E91", {"points": [v(1.35, -3.37) * mm, v(-1.78, -3.91) * mm, v(-4.58, -4.59) * mm, v(-5.62, -4.88) * mm], "startDerivative": vector(-7.37, -1.63) * mm, "endDerivative": vector(-3.26, -0.72) * mm});
            skFitSpline(sketch, "E92", {"points": [v(-5.62, -4.88) * mm, v(-6.85, -6.36) * mm, v(-7.27, -7.04) * mm], "startDerivative": vector(-3.23, -2.97) * mm, "endDerivative": vector(-0.98, -2.16) * mm});
            skFitSpline(sketch, "E93", {"points": [v(-7.27, -7.04) * mm, v(-5.63, -6.33) * mm, v(-3, -5.67) * mm, v(-1.44, -5.45) * mm, v(-0.22, -5.4) * mm, v(1.56, -5.48) * mm], "startDerivative": vector(7.92, 4.9) * mm, "endDerivative": vector(8.91, -0.7) * mm});
            skFitSpline(sketch, "E94", {"points": [v(1.56, -5.48) * mm, v(0.2, -6.04) * mm, v(-1, -6.52) * mm, v(-2.2, -7.03) * mm, v(-2.78, -7.4) * mm], "startDerivative": vector(-6.71, -3.14) * mm, "endDerivative": vector(-2.21, -1.92) * mm});
            skFitSpline(sketch, "E95", {"points": [v(-2.78, -7.4) * mm, v(-2.75, -8.44) * mm, v(-2.62, -9.2) * mm], "startDerivative": vector(-0.3, -1.25) * mm, "endDerivative": vector(0.65, -1.4) * mm});
            skFitSpline(sketch, "E96", {"points": [v(-2.62, -9.2) * mm, v(-1.35, -8.08) * mm, v(-0.13, -7.17) * mm, v(1.5, -6.16) * mm, v(3.56, -5.3) * mm, v(5.33, -4.74) * mm], "startDerivative": vector(6.66, 6.06) * mm, "endDerivative": vector(8.63, 2.53) * mm});
            skFitSpline(sketch, "E97", {"points": [v(5.33, -4.74) * mm, v(4.55, -5.68) * mm, v(4.16, -6.15) * mm], "startDerivative": vector(-1.45, -1.73) * mm, "endDerivative": vector(-0.86, -1.04) * mm});
            skFitSpline(sketch, "E98", {"points": [v(4.16, -6.15) * mm, v(4.04, -6.8) * mm, v(4.07, -7.3) * mm], "startDerivative": vector(-0.3, -1.26) * mm, "endDerivative": vector(0.13, -1.03) * mm});
            skFitSpline(sketch, "E99", {"points": [v(4.07, -7.3) * mm, v(4.64, -6.42) * mm, v(6.54, -4.31) * mm, v(8.35, -2.71) * mm, v(10.1, -1.3) * mm, v(11.17, -0.1) * mm, v(11.35, 0.38) * mm], "startDerivative": vector(3.44, 5.95) * mm, "endDerivative": vector(1.15, 4.7) * mm});
            skFitSpline(sketch, "E100", {"points": [v(11.35, 0.38) * mm, v(10.23, 0.38) * mm, v(9.48, 0.1) * mm], "startDerivative": vector(-2.17, 0.17) * mm, "endDerivative": vector(-1.54, -0.77) * mm});
            skFitSpline(sketch, "E101", {"points": [v(9.48, 0.1) * mm, v(9.75, 1.34) * mm, v(10.65, 3.3) * mm, v(11.86, 5.13) * mm], "startDerivative": vector(0.66, 4.27) * mm, "endDerivative": vector(3.45, 4.83) * mm});
            skFitSpline(sketch, "E102", {"points": [v(11.86, 5.13) * mm, v(11.07, 5.52) * mm], "startDerivative": vector(-0.79, 0.4) * mm, "endDerivative": vector(-0.79, 0.4) * mm});
            skFitSpline(sketch, "E103", {"points": [v(11.07, 5.52) * mm, v(10.66, 5.33) * mm, v(9.58, 5.34) * mm, v(8.55, 5.37) * mm, v(8.11, 5.52) * mm], "startDerivative": vector(-1.8, -1.2) * mm, "endDerivative": vector(-1.92, 0.9) * mm});
            skFitSpline(sketch, "E104", {"points": [v(8.11, 5.52) * mm, v(7.66, 6.61) * mm, v(7.33, 7.49) * mm], "startDerivative": vector(-0.9, 2.11) * mm, "endDerivative": vector(-0.66, 1.82) * mm});
            skFitSpline(sketch, "E105", {"points": [v(7.33, 7.49) * mm, v(8.25, 7.33) * mm, v(9.3, 6.85) * mm, v(10.34, 6.19) * mm, v(11.17, 5.73) * mm, v(12.2, 5.26) * mm, v(13.25, 5.42) * mm, v(14.62, 5.93) * mm, v(14.78, 6.3) * mm, v(14.64, 6.65) * mm, v(13.6, 7.28) * mm, v(12.44, 7.98) * mm, v(10.51, 8.75) * mm, v(9.24, 9.07) * mm], "startDerivative": vector(12.72, -1.5) * mm, "endDerivative": vector(-13.9, 3.06) * mm});
            skFitSpline(sketch, "E106", {"points": [v(1.24, 9.41) * mm, v(-0.26, 8.95) * mm, v(-1.16, 8.61) * mm], "startDerivative": vector(-2.85, -0.82) * mm, "endDerivative": vector(-1.9, -0.77) * mm});
            skFitSpline(sketch, "E107", {"points": [v(-1.16, 8.61) * mm, v(-0.28, 8.46) * mm, v(0.33, 8.25) * mm], "startDerivative": vector(1.7, -0.24) * mm, "endDerivative": vector(1.26, -0.48) * mm});
            skFitSpline(sketch, "E108", {"points": [v(0.33, 8.25) * mm, v(-0.9, 8.12) * mm, v(-2.08, 7.76) * mm], "startDerivative": vector(-2.4, -0.13) * mm, "endDerivative": vector(-1.72, -0.78) * mm});
            skFitSpline(sketch, "E109", {"points": [v(-2.08, 7.76) * mm, v(-0.53, 7.34) * mm, v(0.57, 6.14) * mm], "startDerivative": vector(2.67, -0.3) * mm, "endDerivative": vector(2, -2.95) * mm});
            skFitSpline(sketch, "E110", {"points": [v(-1.01, 6.05) * mm, v(-3.51, 5.53) * mm, v(-5.45, 5.07) * mm], "startDerivative": vector(-4.86, -0.96) * mm, "endDerivative": vector(-4, -0.98) * mm});
            skFitSpline(sketch, "E111", {"points": [v(-5.45, 5.07) * mm, v(-4.15, 4.82) * mm, v(-2.8, 4.28) * mm], "startDerivative": vector(2.67, -0.39) * mm, "endDerivative": vector(2.62, -1.2) * mm});
            skFitSpline(sketch, "E112", {"points": [v(-2.8, 4.28) * mm, v(-5.7, 3.85) * mm, v(-8.17, 2.64) * mm], "startDerivative": vector(-5.87, -0.43) * mm, "endDerivative": vector(-4.85, -2.86) * mm});
            skFitSpline(sketch, "E113", {"points": [v(-0.94, 1.13) * mm, v(-2.9, 0.44) * mm, v(-4.39, -0.42) * mm], "startDerivative": vector(-3.89, -1.18) * mm, "endDerivative": vector(-2.98, -1.92) * mm});
            skFitSpline(sketch, "E114", {"points": [v(-4.39, -0.42) * mm, v(-0.94, -0.95) * mm, v(0.6, -1.29) * mm], "startDerivative": vector(6.34, -0.9) * mm, "endDerivative": vector(3.46, -0.83) * mm});
            skFitSpline(sketch, "E115", {"points": [v(0.6, -1.29) * mm, v(-2.61, -2.02) * mm, v(-5.63, -2.93) * mm], "startDerivative": vector(-6.43, -1.36) * mm, "endDerivative": vector(-6.04, -1.95) * mm});
            skFitSpline(sketch, "E116", {"points": [v(-1.17, -3.8) * mm, v(-2.81, -4.56) * mm, v(-3.68, -5) * mm], "startDerivative": vector(-3.08, -1.33) * mm, "endDerivative": vector(-1.88, -0.99) * mm});
            skFitSpline(sketch, "E117", {"points": [v(-3.68, -5) * mm, v(-1.39, -5) * mm, v(1.56, -5.48) * mm], "startDerivative": vector(4.77, 0.2) * mm, "endDerivative": vector(5.69, -1.12) * mm});
            skFitSpline(sketch, "E118", {"points": [v(1.56, -5.48) * mm, v(0.69, -6) * mm], "startDerivative": vector(-0.87, -0.52) * mm, "endDerivative": vector(-0.87, -0.52) * mm});
            skFitSpline(sketch, "E119", {"points": [v(0.69, -6) * mm, v(2.65, -5.18) * mm], "startDerivative": vector(1.97, 0.82) * mm, "endDerivative": vector(1.97, 0.82) * mm});
            skFitSpline(sketch, "E120", {"points": [v(2.65, -5.18) * mm, v(1.36, -5.91) * mm, v(-0.2, -7.22) * mm], "startDerivative": vector(-2.8, -1.4) * mm, "endDerivative": vector(-2.91, -2.66) * mm});
            skFitSpline(sketch, "E121", {"points": [v(5.33, -4.74) * mm, v(5.22, -5) * mm, v(5.16, -5.28) * mm], "startDerivative": vector(-0.23, -0.52) * mm, "endDerivative": vector(-0.1, -0.55) * mm});
            skFitSpline(sketch, "E122", {"points": [v(5.16, -5.28) * mm, v(7.67, -3.07) * mm, v(9.43, -1.87) * mm], "startDerivative": vector(4.65, 4.33) * mm, "endDerivative": vector(3.85, 2.43) * mm});
            skFitSpline(sketch, "E123", {"points": [v(11.86, 5.13) * mm, v(10.85, 4.7) * mm, v(9.64, 4.62) * mm], "startDerivative": vector(-2, -1.08) * mm, "endDerivative": vector(-2.44, 0.06) * mm});
            skFitSpline(sketch, "E124", {"points": [v(9.64, 4.62) * mm, v(10.02, 4.9) * mm, v(10.5, 5.31) * mm], "startDerivative": vector(0.8, 0.56) * mm, "endDerivative": vector(0.91, 0.81) * mm});
            skFitSpline(sketch, "E125", {"points": [v(10.23, 5.07) * mm, v(9.19, 4.98) * mm, v(7.99, 4.99) * mm, v(7.35, 5.46) * mm, v(7.12, 6.1) * mm, v(6.1, 6.72) * mm, v(5.19, 7) * mm], "startDerivative": vector(-5.8, -0.51) * mm, "endDerivative": vector(-5.22, 1.42) * mm});
            skFitSpline(sketch, "E126", {"points": [v(5.19, 7) * mm, v(5.62, 7.4) * mm, v(5.9, 7.53) * mm], "startDerivative": vector(0.78, 0.78) * mm, "endDerivative": vector(0.64, 0.23) * mm});
            skFitSpline(sketch, "E127", {"points": [v(5.9, 7.53) * mm, v(4.97, 7.77) * mm, v(3.45, 7.87) * mm], "startDerivative": vector(-1.96, 0.63) * mm, "endDerivative": vector(-2.9, 0.09) * mm});
            skFitSpline(sketch, "E128", {"points": [v(3.45, 7.87) * mm, v(5.13, 8.13) * mm, v(7.03, 7.96) * mm, v(9.25, 7.19) * mm, v(10.34, 6.19) * mm], "startDerivative": vector(4.4, 2.65) * mm, "endDerivative": vector(2.76, -5.7) * mm});
            skFitSpline(sketch, "E129", {"points": [v(9.74, -2.12) * mm, v(10.3, -3.12) * mm, v(11.48, -4.15) * mm], "startDerivative": vector(0.96, -2.24) * mm, "endDerivative": vector(2.47, -1.83) * mm});
            skFitSpline(sketch, "E130", {"points": [v(11.48, -4.15) * mm, v(10.48, -3.94) * mm, v(9.76, -3.56) * mm], "startDerivative": vector(-2, 0.28) * mm, "endDerivative": vector(-1.44, 0.9) * mm});
            skFitSpline(sketch, "E131", {"points": [v(9.76, -3.56) * mm, v(10.12, -4.94) * mm, v(11.14, -7.13) * mm], "startDerivative": vector(0.64, -3.02) * mm, "endDerivative": vector(2.06, -4.06) * mm});
            skFitSpline(sketch, "E132", {"points": [v(9.74, -2.12) * mm, v(8.89, -2.88) * mm, v(8.24, -3.4) * mm, v(8.2, -3.56) * mm, v(8.16, -3.56) * mm, v(8.18, -3.77) * mm, v(9.2, -5.53) * mm, v(11.14, -7.13) * mm], "startDerivative": vector(-4.6, -4.5) * mm, "endDerivative": vector(7.91, -5.29) * mm});
            skFitSpline(sketch, "E133", {"points": [v(12.02, 5.07) * mm, v(11.6, 4.1) * mm, v(11.01, 2.52) * mm], "startDerivative": vector(-0.85, -1.93) * mm, "endDerivative": vector(-0.63, -3.62) * mm});
            skFitSpline(sketch, "E134", {"points": [v(11.01, 2.52) * mm, v(13.76, 2.77) * mm, v(14.86, 2.66) * mm, v(17.46, 1.48) * mm, v(17.93, 0.93) * mm, v(18.06, 0.15) * mm, v(17.79, -1.08) * mm, v(17.32, -1.79) * mm], "startDerivative": vector(15.58, 1.51) * mm, "endDerivative": vector(-4.47, -5.56) * mm});
            skFitSpline(sketch, "E135", {"points": [v(17.32, -1.79) * mm, v(17.32, -1.14) * mm, v(17, -0.32) * mm, v(15.92, 0.35) * mm, v(14.59, 0.64) * mm, v(13.03, 0.73) * mm, v(11.63, 0.64) * mm, v(10.46, 0.54) * mm, v(9.65, 0.34) * mm, v(9.58, 0.32) * mm], "startDerivative": vector(0.46, 6.78) * mm, "endDerivative": vector(-1.64, -0.38) * mm});
            skFitSpline(sketch, "E136", {"points": [v(9.58, 0.32) * mm, v(9.58, 0.6) * mm, v(9.76, 1.2) * mm, v(10.39, 2.66) * mm, v(11.66, 4.73) * mm, v(11.95, 5.13) * mm, v(12.02, 5.07) * mm], "startDerivative": vector(-0.21, 2.6) * mm, "endDerivative": vector(1.08, -1.54) * mm});
            skSolve(sketch);
        }
        {
            var Q0;
            {var subQ6=sQuery(id+"F7.wireOp",EDGE,"E80");Q0=makeQuery(id+"F7.imprint","IMPRINT",FACE,{"disambiguationData":[TD([[makeQuery(id+"F7.imprint","IMPRINT",EDGE,{"derivedFrom":subQ6}),1.0]])]});}
            extrude(context, id + "F8", {"entities" : qUnion([Q0]), "depth" : 1.2 * mm, "offsetDistance" : 25 * mm});
        }
        {
            var Q0;
            Q0=makeQuery(id+"F7.imprint","IMPRINT",FACE,{"disambiguationData":[TD([[makeQuery(id+"F7.imprint","IMPRINT",EDGE,{"derivedFrom":sQuery(id+"F7.wireOp",EDGE,"E88")}),1.0]])]});
            var Q1;
            {var subQ1=sQuery(id+"F7.wireOp",EDGE,"E92");Q1=makeQuery(id+"F7.imprint","IMPRINT",FACE,{"disambiguationData":[TD([[makeQuery(id+"F7.imprint","IMPRINT",EDGE,{"derivedFrom":subQ1}),1.0]])]});}
            var Q2;
            Q2=makeQuery(id+"F7.imprint","IMPRINT",FACE,{"disambiguationData":[TD([[makeQuery(id+"F7.imprint","IMPRINT",EDGE,{"derivedFrom":sQuery(id+"F7.wireOp",EDGE,"E94")}),1.0]])]});
            var Q3;
            {var subQ2=sQuery(id+"F7.wireOp",EDGE,"E86");Q3=makeQuery(id+"F7.imprint","IMPRINT",FACE,{"disambiguationData":[TD([[makeQuery(id+"F7.imprint","IMPRINT",EDGE,{"derivedFrom":subQ2}),1.0]])]});}
            var Q4;
            {var subQ1=sQuery(id+"F7.wireOp",EDGE,"E83");Q4=makeQuery(id+"F7.imprint","IMPRINT",FACE,{"disambiguationData":[TD([[makeQuery(id+"F7.imprint","IMPRINT",EDGE,{"derivedFrom":subQ1}),1.0]])]});}
            var Q5;
            {var subQ4=sQuery(id+"F7.wireOp",EDGE,"E104");Q5=makeQuery(id+"F7.imprint","IMPRINT",FACE,{"disambiguationData":[TD([[makeQuery(id+"F7.imprint","IMPRINT",EDGE,{"derivedFrom":subQ4}),1.0]])]});}
            var Q6;
            Q6=makeQuery(id+"F7.imprint","IMPRINT",FACE,{"disambiguationData":[TD([[makeQuery(id+"F7.imprint","IMPRINT",EDGE,{"derivedFrom":sQuery(id+"F7.wireOp",EDGE,"E97")}),1.0]])]});
            var Q7;
            Q7=makeQuery(id+"F7.imprint","IMPRINT",FACE,{"disambiguationData":[TD([[makeQuery(id+"F7.imprint","IMPRINT",EDGE,{"derivedFrom":sQuery(id+"F7.wireOp",EDGE,"E129")}),-1.0]])]});
            var Q8;
            Q8=makeQuery(id+"F7.imprint","IMPRINT",FACE,{"disambiguationData":[TD([[makeQuery(id+"F7.imprint","IMPRINT",EDGE,{"derivedFrom":sQuery(id+"F7.wireOp",EDGE,"E133")}),-1.0]])]});
            extrude(context, id + "F9", {"entities" : qUnion([Q0, Q1, Q2, Q3, Q4, Q5, Q6, Q7, Q8]), "depth" : 0.9 * mm, "offsetDistance" : 25 * mm});
        }
    });
